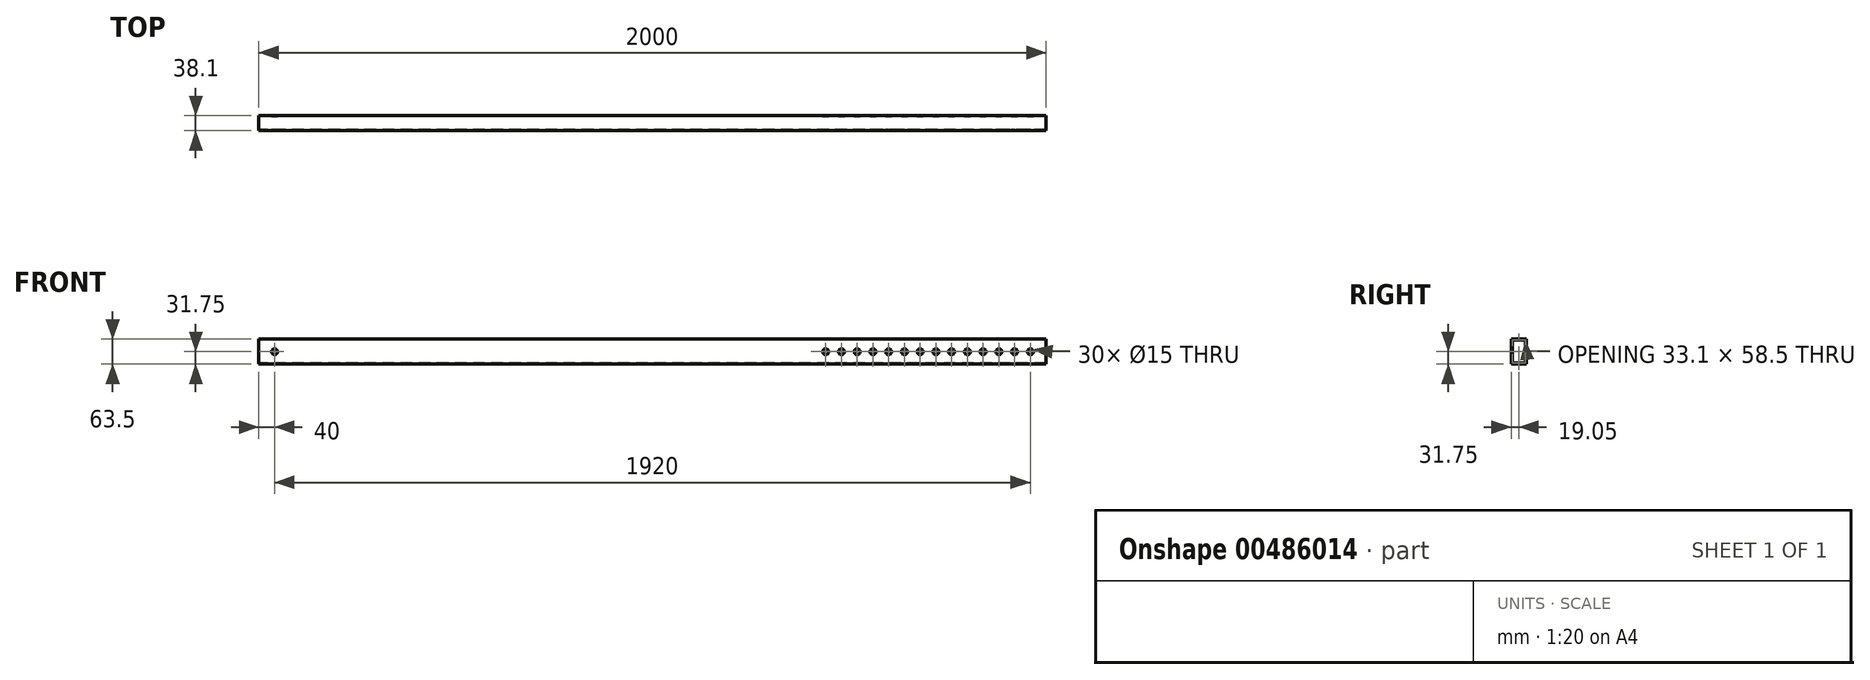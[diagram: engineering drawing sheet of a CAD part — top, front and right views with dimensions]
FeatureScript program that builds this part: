
annotation { "Feature Type Name" : "Feature", "Feature Type Description" : "" }
export const myFeature = defineFeature(function(context is Context, id is Id, definition is map)
    precondition{}
    {
        {
            var Q0;
            Q0=qCreatedBy(makeId("Right.planeOp"),FACE);
            var sketch = newSketch(context, id + "F0", { "sketchPlane" : qUnion([Q0])});
            skLineSegment(sketch, "E0.bottom", {"start": v(19.05, 31.75) * mm, "end": v(-19.05, 31.75) * mm});
            skLineSegment(sketch, "E0.top", {"start": v(19.05, -31.75) * mm, "end": v(-19.05, -31.75) * mm});
            skLineSegment(sketch, "E0.left", {"start": v(19.05, 31.75) * mm, "end": v(19.05, -31.75) * mm});
            skLineSegment(sketch, "E0.right", {"start": v(-19.05, 31.75) * mm, "end": v(-19.05, -31.75) * mm});
            skPoint(sketch, "E0.middle", {"position": v(0, 0) * mm});
            skLineSegment(sketch, "E1.bottom", {"start": v(14.55, 29.25) * mm, "end": v(-14.55, 29.25) * mm});
            skLineSegment(sketch, "E1.top", {"start": v(14.55, -29.25) * mm, "end": v(-14.55, -29.25) * mm});
            skLineSegment(sketch, "E1.left", {"start": v(16.55, 27.25) * mm, "end": v(16.55, -27.25) * mm});
            skLineSegment(sketch, "E1.right", {"start": v(-16.55, 27.25) * mm, "end": v(-16.55, -27.25) * mm});
            skPoint(sketch, "E2.visualSharp", {"position": v(-16.55, 29.25) * mm});
            skArc(sketch, "E2.filletArc", {"start": v(-14.55, 29.25) * mm, "mid": v(-15.96, 28.66) * mm, "end": v(-16.55, 27.25) * mm});
            skPoint(sketch, "E3.visualSharp", {"position": v(16.55, 29.25) * mm});
            skArc(sketch, "E3.filletArc", {"start": v(16.55, 27.25) * mm, "mid": v(15.96, 28.66) * mm, "end": v(14.55, 29.25) * mm});
            skPoint(sketch, "E4.visualSharp", {"position": v(16.55, -29.25) * mm});
            skArc(sketch, "E4.filletArc", {"start": v(14.55, -29.25) * mm, "mid": v(15.96, -28.66) * mm, "end": v(16.55, -27.25) * mm});
            skPoint(sketch, "E5.visualSharp", {"position": v(-16.55, -29.25) * mm});
            skArc(sketch, "E5.filletArc", {"start": v(-16.55, -27.25) * mm, "mid": v(-15.96, -28.66) * mm, "end": v(-14.55, -29.25) * mm});
            skSolve(sketch);
        }
        {
            var Q0;
            Q0 = qSketchRegion(id + "F0", true);
            extrude(context, id + "F1", {"entities" : qUnion([Q0]), "depth" : 2000 * mm});
        }
        {
            var Q0;
            Q0=makeQuery(id+"F1.opExtrude","SWEPT_FACE",FACE,{"disambiguationData":[OSD([sQuery(id+"F0.wireOp",EDGE,"E0.right")])]});
            var sketch = newSketch(context, id + "F2", { "sketchPlane" : qUnion([Q0])});
            skCircle(sketch, "E6", {"center": v(40, 0) * mm, "radius": 7.5 * mm});
            skPoint(sketch, "E6.centerSnap0", {"position": v(0, 0) * mm});
            skSolve(sketch);
        }
        {
            var Q0;
            Q0 = qSketchRegion(id + "F2", true);
            var Q1;
            Q1=makeQuery(id+"F1.opExtrude","SWEPT_FACE",FACE,{"disambiguationData":[OSD([sQuery(id+"F0.wireOp",EDGE,"E0.left")])]});
            extrude(context, id + "F3", {"entities" : qUnion([Q0]), "operationType" : NewBodyOperationType.REMOVE, "endBound" : BoundingType.UP_TO_SURFACE, "oppositeDirection" : true, "endBoundEntityFace" : qUnion([Q1]), "depth" : 25 * mm});
        }
        {
            var Q0;
            Q0=makeQuery(id+"F1.opExtrude","SWEPT_FACE",FACE,{"disambiguationData":[OSD([sQuery(id+"F0.wireOp",EDGE,"E0.right")])]});
            var sketch = newSketch(context, id + "F4", { "sketchPlane" : qUnion([Q0])});
            skCircle(sketch, "E7", {"center": v(1960, 0) * mm, "radius": 7.5 * mm});
            skPoint(sketch, "E7.centerSnap0", {"position": v(2000, 0) * mm});
            skCircle(sketch, "E8", {"center": v(1920, 0) * mm, "radius": 7.5 * mm});
            skCircle(sketch, "E9", {"center": v(1880, 0) * mm, "radius": 7.5 * mm});
            skCircle(sketch, "E10", {"center": v(1840, 0) * mm, "radius": 7.5 * mm});
            skCircle(sketch, "E11", {"center": v(1800, 0) * mm, "radius": 7.5 * mm});
            skCircle(sketch, "E12", {"center": v(1760, 0) * mm, "radius": 7.5 * mm});
            skCircle(sketch, "E13", {"center": v(1720, 0) * mm, "radius": 7.5 * mm});
            skCircle(sketch, "E14", {"center": v(1680, 0) * mm, "radius": 7.5 * mm});
            skCircle(sketch, "E15", {"center": v(1640, 0) * mm, "radius": 7.5 * mm});
            skCircle(sketch, "E16", {"center": v(1600, 0) * mm, "radius": 7.5 * mm});
            skCircle(sketch, "E17", {"center": v(1560, 0) * mm, "radius": 7.5 * mm});
            skCircle(sketch, "E18", {"center": v(1520, 0) * mm, "radius": 7.5 * mm});
            skCircle(sketch, "E19", {"center": v(1480, 0) * mm, "radius": 7.5 * mm});
            skCircle(sketch, "E20", {"center": v(1440, 0) * mm, "radius": 7.5 * mm});
            skLineSegment(sketch, "E21", {"start": v(2000, 0) * mm, "end": v(1342.41, 0) * mm});
            skSolve(sketch);
        }
        {
            var Q0;
            Q0 = qSketchRegion(id + "F4", true);
            var Q1;
            Q1=makeQuery(id+"F1.opExtrude","SWEPT_FACE",FACE,{"disambiguationData":[OSD([sQuery(id+"F0.wireOp",EDGE,"E0.left")])]});
            extrude(context, id + "F5", {"entities" : qUnion([Q0]), "operationType" : NewBodyOperationType.REMOVE, "endBound" : BoundingType.UP_TO_SURFACE, "oppositeDirection" : true, "endBoundEntityFace" : qUnion([Q1]), "depth" : 25 * mm});
        }
    });
